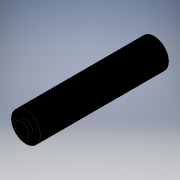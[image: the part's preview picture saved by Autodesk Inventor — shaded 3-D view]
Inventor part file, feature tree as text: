
AUTODESK INVENTOR PART (.ipt)
format: ipt  version: 2018 (Build 220112000, 112)  size: 104,448 bytes
history: native  units: in
note: dims shown in document units (in); Inventor stores cm internally (conversion verified against a paired STEP export)
features: extrude x3, sketch x3
ambient origin geometry x8: Origin, YZ Plane, XZ Plane, XY Plane, X Axis, Y Axis, Z Axis, Center Point
bodies: Solid1 (feature_tree)
feature tree (6):
  extrude  "Extrusion1"  Depth=11.0in TaperAngle=0.0deg
  extrude  "Extrusion2"  Depth=0.35in TaperAngle=0.0deg
  extrude  "Extrusion3"  Depth=0.35in TaperAngle=0.0deg
  sketch  "Sketch1"  dims[d0=2.5in d1=11.0in d2=0.0in]
  sketch  "Sketch2"  dims[d3=1.16in d4=0.35in d5=0.0in]
  sketch  "Sketch3"  dims[d6=1.16in d7=0.35in d8=0.0in]
